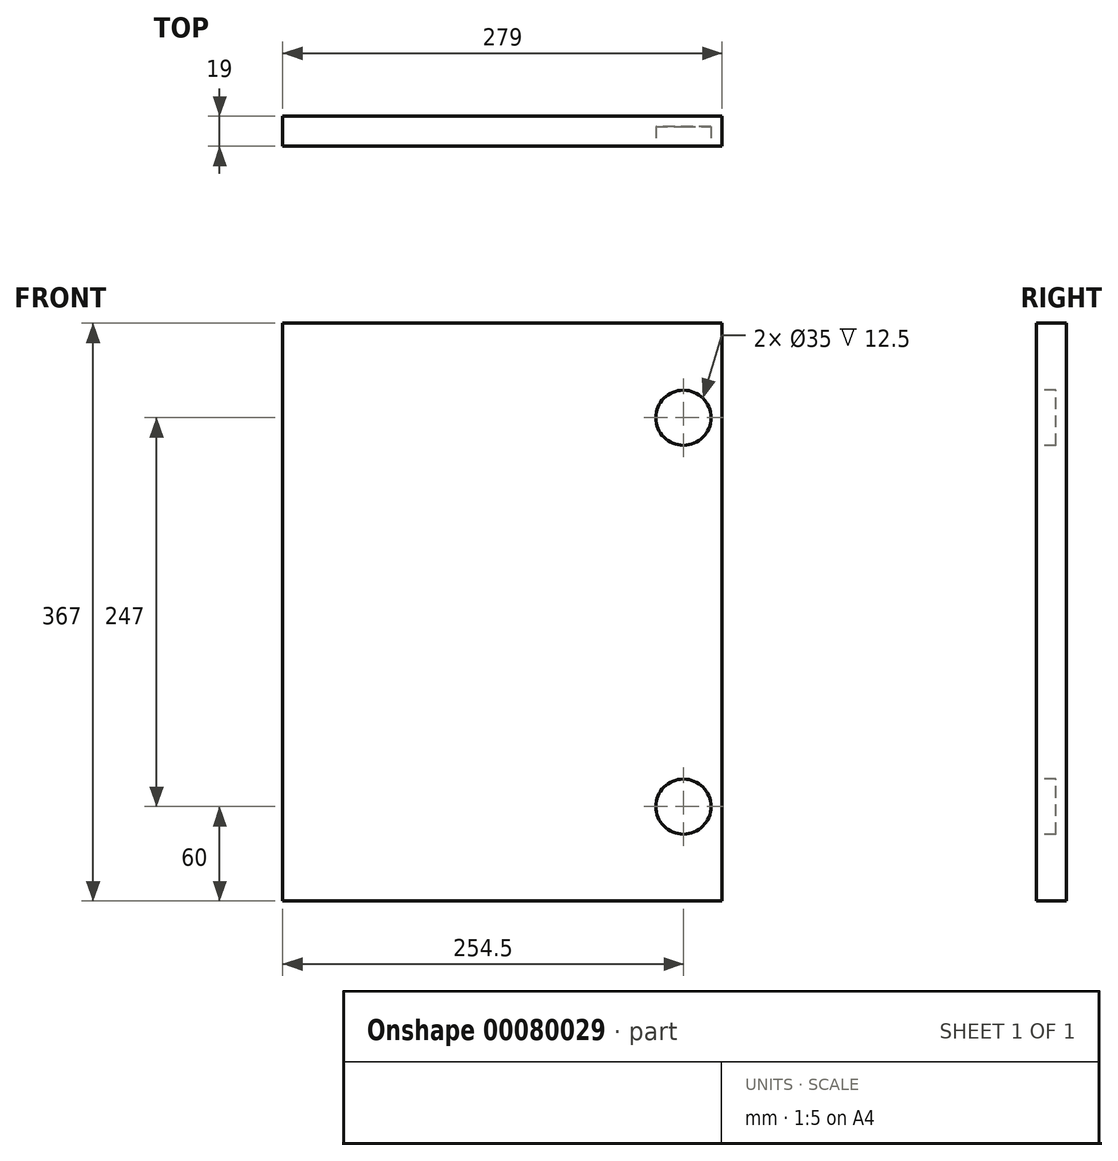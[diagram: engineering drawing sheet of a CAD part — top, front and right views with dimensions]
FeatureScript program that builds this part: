
annotation { "Feature Type Name" : "Feature", "Feature Type Description" : "" }
export const myFeature = defineFeature(function(context is Context, id is Id, definition is map)
    precondition{}
    {
        {
            var Q0;
            Q0=qCreatedBy(makeId("Front.planeOp"),FACE);
            var sketch = newSketch(context, id + "F0", { "sketchPlane" : qUnion([Q0])});
            skLineSegment(sketch, "E0.bottom", {"start": v(0, 0) * mm, "end": v(279, 0) * mm});
            skLineSegment(sketch, "E0.top", {"start": v(0, -367) * mm, "end": v(279, -367) * mm});
            skLineSegment(sketch, "E0.left", {"start": v(0, 0) * mm, "end": v(0, -367) * mm});
            skLineSegment(sketch, "E0.right", {"start": v(279, 0) * mm, "end": v(279, -367) * mm});
            skSolve(sketch);
        }
        {
            var Q0;
            Q0=makeQuery(id+"F0.imprint","IMPRINT",FACE,{"disambiguationData":[TD([[makeQuery(id+"F0.imprint","IMPRINT",EDGE,{"derivedFrom":sQuery(id+"F0.wireOp",EDGE,"E0.bottom")}),-1.0]])]});
            extrude(context, id + "F1", {"entities" : qUnion([Q0]), "depth" : 19 * mm});
        }
        {
            var Q0;
            Q0=makeQuery(id+"F1.opExtrude","CAP_FACE",FACE,{"disambiguationData":[OSD([sQuery(id+"F0.wireOp",EDGE,"E0.bottom"),sQuery(id+"F0.wireOp",EDGE,"E0.top"),sQuery(id+"F0.wireOp",EDGE,"E0.left"),sQuery(id+"F0.wireOp",EDGE,"E0.right")])],"isStart":false});
            var sketch = newSketch(context, id + "F2", { "sketchPlane" : qUnion([Q0])});
            skCircle(sketch, "E1", {"center": v(254.5, -60) * mm, "radius": 17.5 * mm});
            skCircle(sketch, "E2", {"center": v(254.5, -307) * mm, "radius": 17.5 * mm});
            skSolve(sketch);
        }
        {
            var Q0;
            Q0=makeQuery(id+"F2.imprint","IMPRINT",FACE,{"disambiguationData":[TD([[makeQuery(id+"F2.imprint","IMPRINT",EDGE,{"derivedFrom":sQuery(id+"F2.wireOp",EDGE,"E1")}),1.0]])]});
            var Q1;
            Q1=makeQuery(id+"F2.imprint","IMPRINT",FACE,{"disambiguationData":[TD([[makeQuery(id+"F2.imprint","IMPRINT",EDGE,{"derivedFrom":sQuery(id+"F2.wireOp",EDGE,"E2")}),1.0]])]});
            var Q2;
            Q2=sQuery(id+"F2.wireOp",EDGE,"E2");
            var Q3;
            Q3=sQuery(id+"F2.wireOp",EDGE,"E1");
            extrude(context, id + "F3", {"entities" : qUnion([Q0, Q1]), "operationType" : NewBodyOperationType.REMOVE, "surfaceEntities" : qUnion([Q2, Q3]), "oppositeDirection" : true, "depth" : 12.5 * mm});
        }
    });
